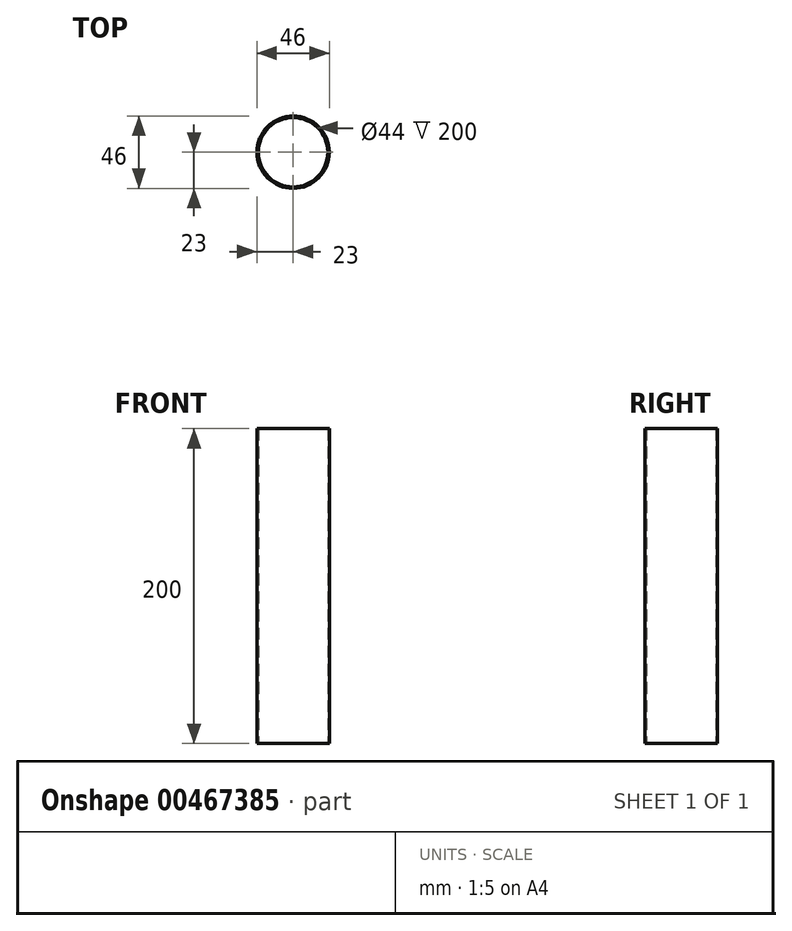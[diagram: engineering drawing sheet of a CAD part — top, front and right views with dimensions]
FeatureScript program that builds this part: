
annotation { "Feature Type Name" : "Feature", "Feature Type Description" : "" }
export const myFeature = defineFeature(function(context is Context, id is Id, definition is map)
    precondition{}
    {
        {
            var Q0;
            Q0=qCreatedBy(makeId("Top.planeOp"),FACE);
            var sketch = newSketch(context, id + "F0", { "sketchPlane" : qUnion([Q0])});
            skCircle(sketch, "E0", {"center": v(0, 0) * mm, "radius": 22 * mm});
            skCircle(sketch, "E1.0", {"center": v(0, 0) * mm, "radius": 23 * mm});
            skSolve(sketch);
        }
        {
            var Q0;
            Q0 = qSketchRegion(id + "F0", true);
            extrude(context, id + "F1", {"entities" : qUnion([Q0]), "depth" : 200 * mm});
        }
    });
